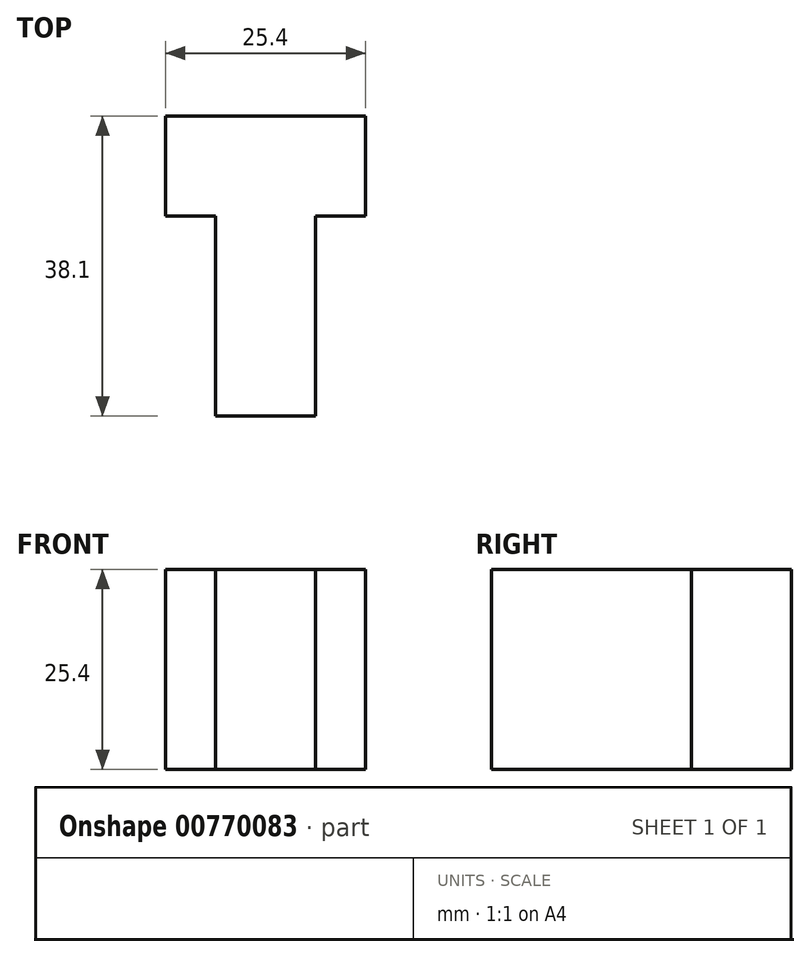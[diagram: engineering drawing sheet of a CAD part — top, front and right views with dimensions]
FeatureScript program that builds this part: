
annotation { "Feature Type Name" : "Feature", "Feature Type Description" : "" }
export const myFeature = defineFeature(function(context is Context, id is Id, definition is map)
    precondition{}
    {
        {
            var Q0;
            Q0=qCreatedBy(makeId("Top.planeOp"),FACE);
            var sketch = newSketch(context, id + "F0", { "sketchPlane" : qUnion([Q0])});
            skLineSegment(sketch, "E0", {"start": v(0, 0) * mm, "end": v(25.4, 0) * mm});
            skLineSegment(sketch, "E1", {"start": v(25.4, 0) * mm, "end": v(25.4, -12.7) * mm});
            skLineSegment(sketch, "E2", {"start": v(0, 0) * mm, "end": v(0, -12.7) * mm});
            skLineSegment(sketch, "E3", {"start": v(0, -12.7) * mm, "end": v(6.35, -12.7) * mm});
            skLineSegment(sketch, "E4", {"start": v(25.4, -12.7) * mm, "end": v(19.05, -12.7) * mm});
            skLineSegment(sketch, "E5", {"start": v(6.35, -12.7) * mm, "end": v(6.35, -38.1) * mm});
            skLineSegment(sketch, "E6", {"start": v(19.05, -12.7) * mm, "end": v(19.05, -38.1) * mm});
            skLineSegment(sketch, "E7", {"start": v(19.05, -38.1) * mm, "end": v(6.35, -38.1) * mm});
            skSolve(sketch);
        }
        {
            var Q0;
            Q0 = qSketchRegion(id + "F0", true);
            extrude(context, id + "F1", {"entities" : qUnion([Q0]), "depth" : 25.4 * mm, "offsetDistance" : 25.4 * mm});
        }
    });
